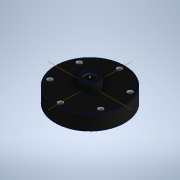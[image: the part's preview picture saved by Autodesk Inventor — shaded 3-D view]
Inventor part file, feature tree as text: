
AUTODESK INVENTOR PART (.ipt)
format: ipt  version: 2021.1 (Build 251245000, 245)  size: 180,736 bytes
history: native  units: in
note: dims shown in document units (in); Inventor stores cm internally (conversion verified against a paired STEP export)
features: sketch x8, extrude x7, thread x2
ambient origin geometry x8: Origin, YZ Plane, XZ Plane, XY Plane, X Axis, Y Axis, Z Axis, Center Point
bodies: Solid1 (feature_tree)
feature tree (17):
  extrude  "Extrusion1"  Depth=2.4in
  extrude  "Extrusion2"  Depth=2.0in
  sketch  "Sketch3"  dims[d5=1.0in d6=0.0in d7=0.5in]
  sketch  "Sketch4"  dims[d8=1.4in d9=0.25in d10=0.0in]
  extrude  "Extrusion3"  Depth=1.0in
  extrude  "Extrusion6"  Depth=0.25in TaperAngle=0.0deg
  extrude  "Extrusion7"  Depth=6.6in
  extrude  "Extrusion8"  Depth=1.4in
  thread  "Thread1"  [1 undecoded]
  sketch  "Sketch8"  dims[d22=0.0in d23=0.0in d24=1.324in d25=0.0in d26=7.8in]
  extrude  "Extrusion9"  Depth=1.324in TaperAngle=0.0deg
  thread  "Thread2"  [1 undecoded]
  sketch  "Sketch1"  dims[d0=9.2in d1=2.4in]
  sketch  "Sketch2"  dims[d2=2.0in d3=0.0in d4=2.4in]
  sketch  "Sketch5"  dims[d15=0.0in d16=0.0in d17=6.6in]
  sketch  "Sketch7"  dims[d18=1.4in d19=0.0in d20=0.8in d21=0.8in]
  sketch  "Sketch9"  dims[d27=60.0deg d28=0.7in d29=2.3622in d31=360.0deg d33=0.0in d34=0.0in d35=0.25in d36=0.0in d13=0.5in d14=0.0344in]
note: 2 required parameter values undecoded (feature->parameter linkage not recoverable at this tier; creation-order binding heuristic only, values carry confidence <= 0.55)
